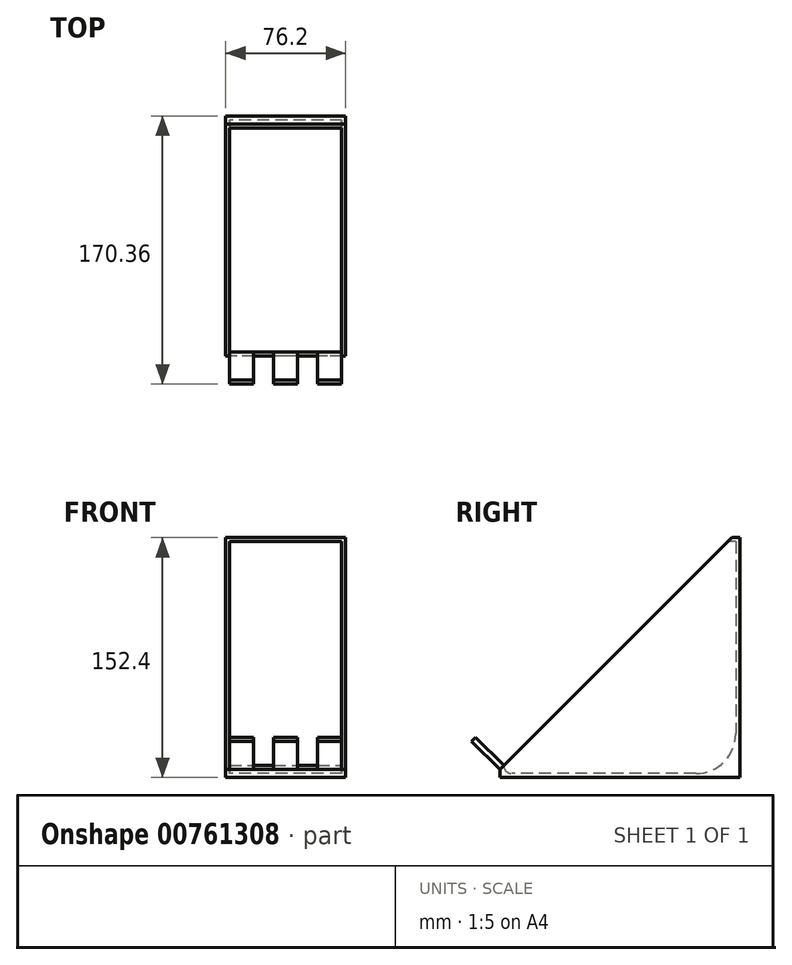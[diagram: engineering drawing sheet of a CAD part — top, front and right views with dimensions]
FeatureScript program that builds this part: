
annotation { "Feature Type Name" : "Feature", "Feature Type Description" : "" }
export const myFeature = defineFeature(function(context is Context, id is Id, definition is map)
    precondition{}
    {
        {
            var Q0;
            Q0=qCreatedBy(makeId("Top.planeOp"),FACE);
            var sketch = newSketch(context, id + "F0", { "sketchPlane" : qUnion([Q0])});
            skLineSegment(sketch, "E0.bottom", {"start": v(38.1, 76.2) * mm, "end": v(-38.1, 76.2) * mm});
            skLineSegment(sketch, "E0.top", {"start": v(38.1, -76.2) * mm, "end": v(-38.1, -76.2) * mm});
            skLineSegment(sketch, "E0.left", {"start": v(38.1, 76.2) * mm, "end": v(38.1, -76.2) * mm});
            skLineSegment(sketch, "E0.right", {"start": v(-38.1, 76.2) * mm, "end": v(-38.1, -76.2) * mm});
            skPoint(sketch, "E0.middle", {"position": v(0, 0) * mm});
            skSolve(sketch);
        }
        {
            var Q0;
            Q0 = qSketchRegion(id + "F0", true);
            extrude(context, id + "F1", {"entities" : qUnion([Q0]), "depth" : 152.4 * mm, "offsetDistance" : 25.4 * mm});
        }
        {
            var Q0;
            Q0=makeQuery(id+"F1.opExtrude","CAP_EDGE",EDGE,{"disambiguationData":[OSD([sQuery(id+"F0.wireOp",EDGE,"E0.top")])],"isStart":false});
            chamfer(context, id + "F2", {"entities" : qUnion([Q0]), "width" : 147.32 * mm, "tangentPropagation" : true});
        }
        {
            var Q0;
            Q0=makeQuery(id+"F2.opChamfer","BLEND_FACE",FACE,{"disambiguationData":[OSD([sQuery(id+"F0.wireOp",EDGE,"E0.top")])]});
            shell(context, id + "F3", {"entities" : qUnion([Q0]), "thickness" : 2.54 * mm});
        }
        {
            var Q0;
            {var subQ0=sQuery(id+"F0.wireOp",EDGE,"E0.bottom");Q0=makeQuery(id+"F3.opShell","OFFSET_EDGE",EDGE,{"disambiguationData":[OSD([subQ0]),TDD([makeQuery(id+"F1.opExtrude","CAP_EDGE",EDGE,{"disambiguationData":[OSD([subQ0])],"isStart":true})])]});}
            fillet(context, id + "F4", {"entities" : qUnion([Q0]), "radius" : 25.4 * mm, "tangentPropagation" : true, "allowEdgeOverflow" : false});
        }
        {
            var Q0;
            {var subQ0=sQuery(id+"F0.wireOp",EDGE,"E0.top");Q0=makeQuery(id+"F3.opShell","OFFSET_EDGE",EDGE,{"disambiguationData":[OSD([subQ0]),TDD([makeQuery(id+"F1.opExtrude","CAP_EDGE",EDGE,{"disambiguationData":[OSD([subQ0])],"isStart":true})])]});}
            fillet(context, id + "F5", {"entities" : qUnion([Q0]), "radius" : 5.08 * mm, "tangentPropagation" : true, "allowEdgeOverflow" : false});
        }
        {
            var Q0;
            Q0=makeQuery(id+"F2.opChamfer","BLEND_FACE",FACE,{"disambiguationData":[OSD([sQuery(id+"F0.wireOp",EDGE,"E0.top")])]});
            var sketch = newSketch(context, id + "F6", { "sketchPlane" : qUnion([Q0])});
            skLineSegment(sketch, "E1.bottom", {"start": v(-35.56, -46.7) * mm, "end": v(-20.32, -46.7) * mm});
            skLineSegment(sketch, "E1.top", {"start": v(-35.56, -50.29) * mm, "end": v(-20.32, -50.29) * mm});
            skLineSegment(sketch, "E1.left", {"start": v(-35.56, -46.7) * mm, "end": v(-35.56, -50.29) * mm});
            skLineSegment(sketch, "E1.right", {"start": v(-20.32, -46.7) * mm, "end": v(-20.32, -50.29) * mm});
            skLineSegment(sketch, "E2.bottom", {"start": v(35.56, -46.7) * mm, "end": v(20.32, -46.7) * mm});
            skLineSegment(sketch, "E2.top", {"start": v(35.56, -50.29) * mm, "end": v(20.32, -50.29) * mm});
            skLineSegment(sketch, "E2.left", {"start": v(35.56, -46.7) * mm, "end": v(35.56, -50.29) * mm});
            skLineSegment(sketch, "E2.right", {"start": v(20.32, -46.7) * mm, "end": v(20.32, -50.29) * mm});
            skLineSegment(sketch, "E3.bottom", {"start": v(-7.58, -46.7) * mm, "end": v(7.66, -46.7) * mm});
            skLineSegment(sketch, "E3.top", {"start": v(-7.58, -50.29) * mm, "end": v(7.66, -50.29) * mm});
            skLineSegment(sketch, "E3.left", {"start": v(-7.58, -46.7) * mm, "end": v(-7.58, -50.29) * mm});
            skLineSegment(sketch, "E3.right", {"start": v(7.66, -46.7) * mm, "end": v(7.66, -50.29) * mm});
            skSolve(sketch);
        }
        {
            var Q0;
            Q0 = qSketchRegion(id + "F6", true);
            extrude(context, id + "F7", {"entities" : qUnion([Q0]), "operationType" : NewBodyOperationType.ADD, "depth" : 25.4 * mm, "offsetDistance" : 25.4 * mm});
        }
    });
